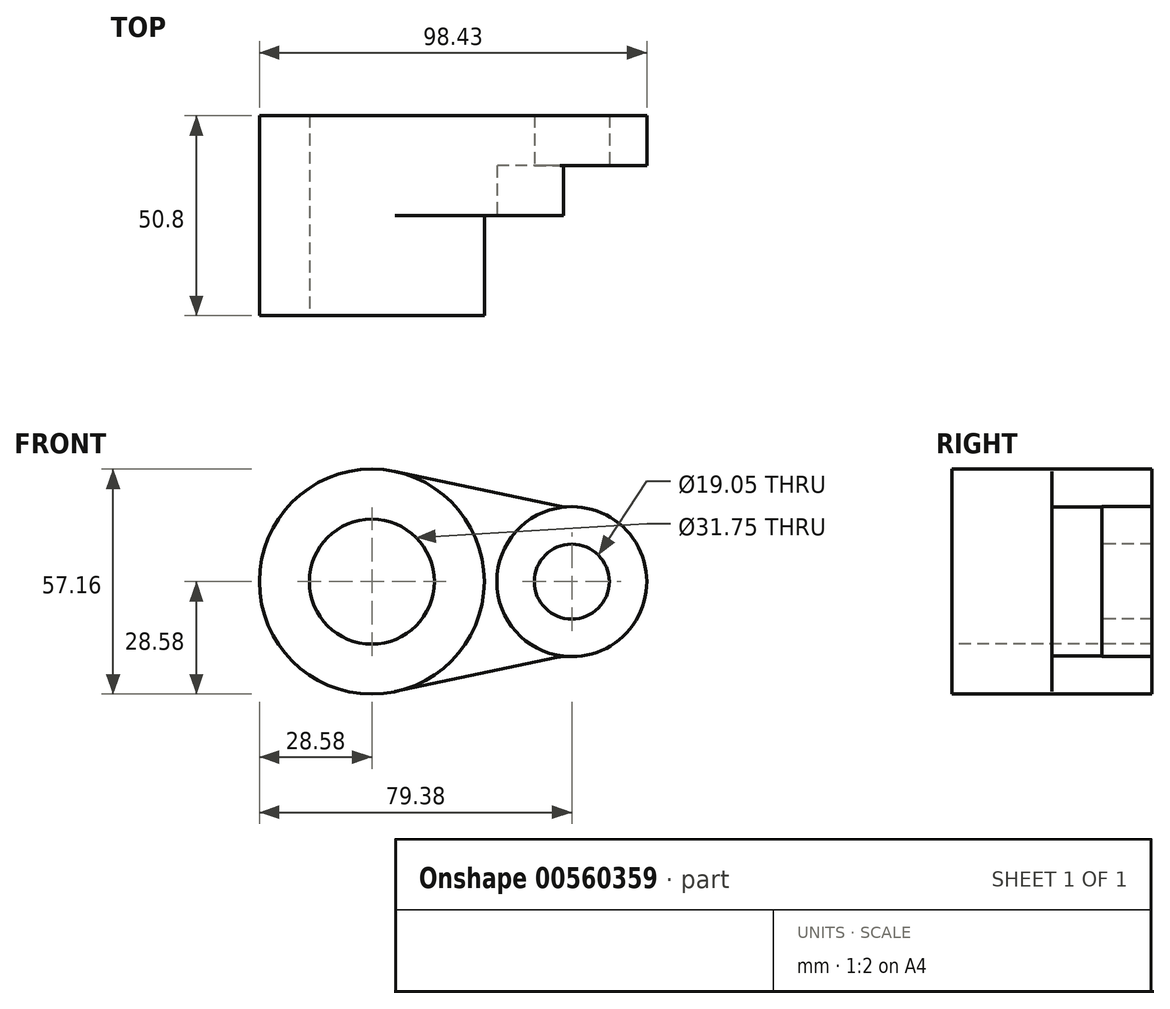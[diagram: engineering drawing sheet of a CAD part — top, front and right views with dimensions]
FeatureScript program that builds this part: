
annotation { "Feature Type Name" : "Feature", "Feature Type Description" : "" }
export const myFeature = defineFeature(function(context is Context, id is Id, definition is map)
    precondition{}
    {
        {
            var Q0;
            Q0=qCreatedBy(makeId("Front.planeOp"),FACE);
            var sketch = newSketch(context, id + "F0", { "sketchPlane" : qUnion([Q0])});
            skCircle(sketch, "E0", {"center": v(0, 0) * mm, "radius": 28.58 * mm});
            skCircle(sketch, "E1", {"center": v(0, 0) * mm, "radius": 15.88 * mm});
            skCircle(sketch, "E2", {"center": v(50.8, 0) * mm, "radius": 19.05 * mm});
            skCircle(sketch, "E3", {"center": v(50.8, 0) * mm, "radius": 9.53 * mm});
            skLineSegment(sketch, "E4", {"start": v(5.9, -27.96) * mm, "end": v(48.67, -18.93) * mm});
            skLineSegment(sketch, "E5", {"start": v(48.67, 18.93) * mm, "end": v(5.9, 27.96) * mm});
            skSolve(sketch);
        }
        {
            var Q0;
            Q0 = qSketchRegion(id + "F0", true);
            extrude(context, id + "F1", {"entities" : qUnion([Q0]), "oppositeDirection" : true, "depth" : 25.4 * mm, "offsetDistance" : 25.4 * mm});
        }
        {
            var Q0;
            Q0=makeQuery(id+"F0.imprint","IMPRINT",FACE,{"disambiguationData":[TD([[makeQuery(id+"F0.imprint","IMPRINT",EDGE,{"derivedFrom":sQuery(id+"F0.wireOp",EDGE,"E1")}),-1.0]])]});
            extrude(context, id + "F2", {"entities" : qUnion([Q0]), "operationType" : NewBodyOperationType.ADD, "depth" : 25.4 * mm, "offsetDistance" : 25.4 * mm});
        }
        {
            var Q0;
            Q0=makeQuery(id+"F0.imprint","IMPRINT",FACE,{"disambiguationData":[TD([[makeQuery(id+"F0.imprint","IMPRINT",EDGE,{"derivedFrom":sQuery(id+"F0.wireOp",EDGE,"E3")}),-1.0]])]});
            extrude(context, id + "F3", {"entities" : qUnion([Q0]), "operationType" : NewBodyOperationType.REMOVE, "oppositeDirection" : true, "depth" : 12.7 * mm, "offsetDistance" : 25.4 * mm});
        }
        {
            var Q0;
            {var subQ0=sQuery(id+"F0.wireOp",EDGE,"E4");var subQ1=sQuery(id+"F0.wireOp",EDGE,"E2");Q0=makeQuery(id+"F3.boolean.opBoolean","SPLIT",EDGE,{"disambiguationData":[topologyDisambiguationEdgeConnected([makeQuery(id+"F3.opExtrude","SWEPT_FACE",FACE,{"disambiguationData":[OSD([subQ1])]})])],"derivedFrom":makeQuery(id+"F1.opExtrude","SWEPT_EDGE",EDGE,{"disambiguationData":[OSD([subQ1,subQ0])]})});}
            var Q1;
            {var subQ0=sQuery(id+"F0.wireOp",EDGE,"E5");var subQ1=sQuery(id+"F0.wireOp",EDGE,"E2");Q1=makeQuery(id+"F3.boolean.opBoolean","SPLIT",EDGE,{"disambiguationData":[topologyDisambiguationEdgeConnected([makeQuery(id+"F3.opExtrude","SWEPT_FACE",FACE,{"disambiguationData":[OSD([subQ1])]})])],"derivedFrom":makeQuery(id+"F1.opExtrude","SWEPT_EDGE",EDGE,{"disambiguationData":[OSD([subQ1,subQ0])]})});}
            fillet(context, id + "F4", {"entities" : qUnion([Q0, Q1]), "radius" : 6.35 * mm, "tangentPropagation" : true, "allowEdgeOverflow" : false});
        }
    });
